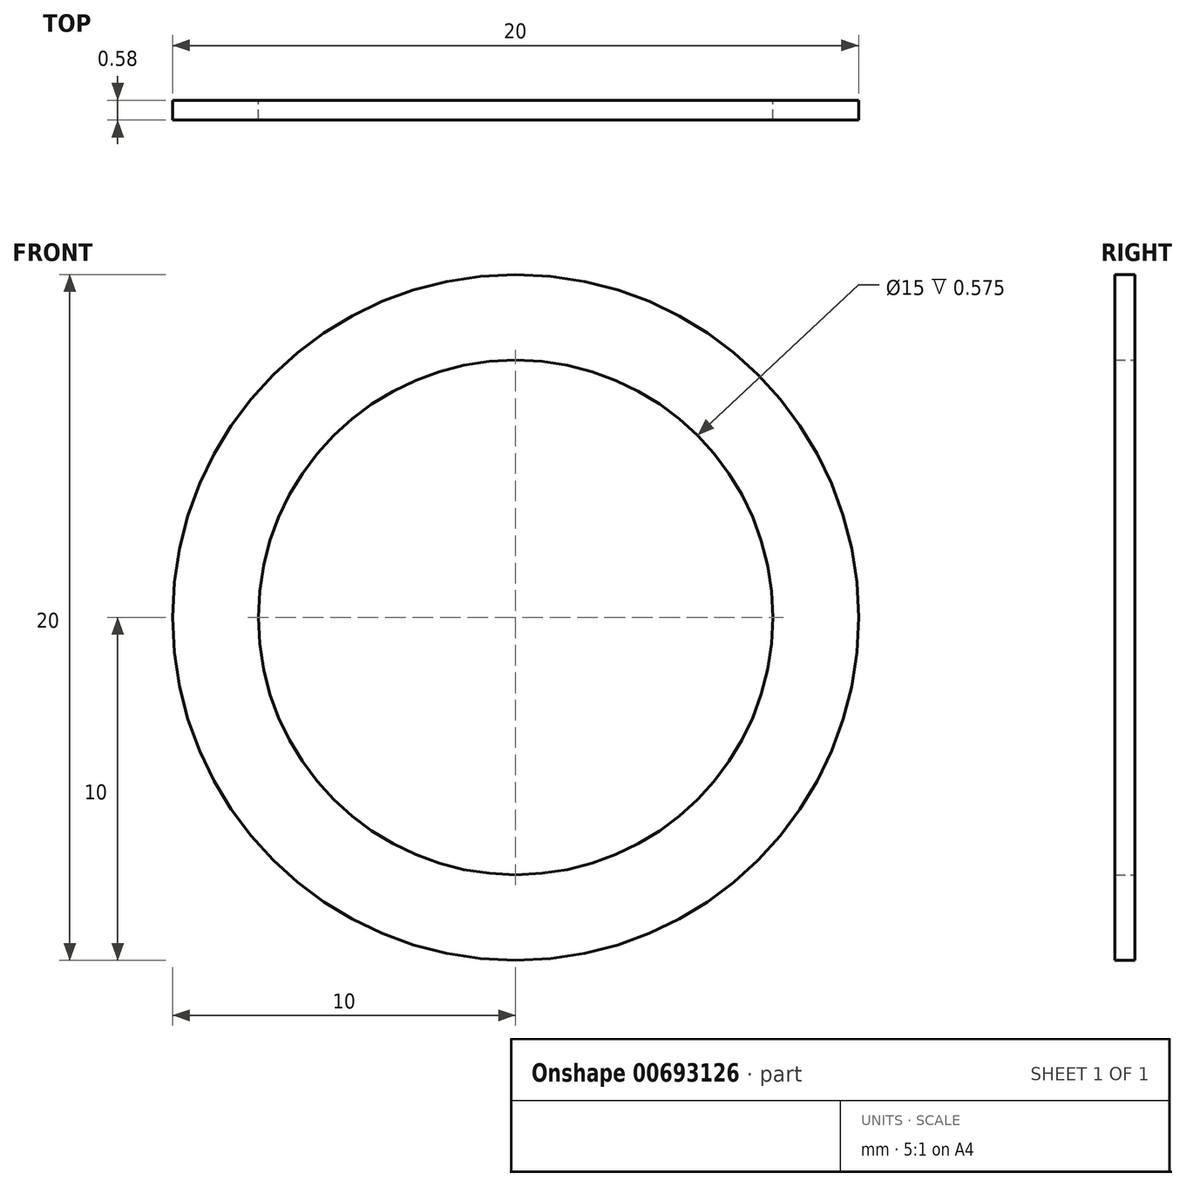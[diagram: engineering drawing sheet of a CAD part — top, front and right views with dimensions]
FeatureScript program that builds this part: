
annotation { "Feature Type Name" : "Feature", "Feature Type Description" : "" }
export const myFeature = defineFeature(function(context is Context, id is Id, definition is map)
    precondition{}
    {
        {
            var Q0;
            Q0=qCreatedBy(makeId("Front.planeOp"),FACE);
            var sketch = newSketch(context, id + "F0", { "sketchPlane" : qUnion([Q0])});
            skCircle(sketch, "E0", {"center": v(0, 0) * mm, "radius": 10 * mm});
            skCircle(sketch, "E1", {"center": v(0, 0) * mm, "radius": 7.5 * mm});
            skSolve(sketch);
        }
        {
            var Q0;
            Q0=makeQuery(id+"F0.imprint","IMPRINT",FACE,{"disambiguationData":[TD([[makeQuery(id+"F0.imprint","IMPRINT",EDGE,{"derivedFrom":sQuery(id+"F0.wireOp",EDGE,"E0")}),1.0]])]});
            extrude(context, id + "F1", {"entities" : qUnion([Q0]), "depth" : 0.57 * mm, "offsetDistance" : 25 * mm});
        }
    });
